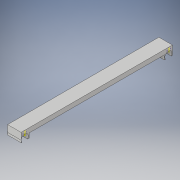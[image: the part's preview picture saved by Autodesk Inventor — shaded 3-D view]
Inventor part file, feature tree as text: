
AUTODESK INVENTOR PART (.ipt)
format: ipt  version: 2018 (Build 220112000, 112)  size: 140,288 bytes
history: native  units: in
note: dims shown in document units (in); Inventor stores cm internally (conversion verified against a paired STEP export)
features: sketch x7, extrude x4, hole x1
ambient origin geometry x8: Origin, YZ Plane, XZ Plane, XY Plane, X Axis, Y Axis, Z Axis, Center Point
bodies: Solid1 (feature_tree)
feature tree (12):
  extrude  "Extrusion1"  Depth=0.375in
  sketch  "Sketch2"  dims[d2=0.125in d3=0.0in d4=0.1in d5=0.0in]
  extrude  "Extrusion2"  Depth=0.1in TaperAngle=0.0deg
  sketch  "Sketch4"  dims[d9=0.22in d10=0.125in d11=0.0in]
  extrude  "Extrusion3"  Depth=0.22in
  extrude  "Extrusion4"  Depth=0.125in TaperAngle=0.0deg
  hole  "Hole1"  [1 undecoded]
  sketch  "Sketch1"  dims[d0=0.375in d1=4.0in]
  sketch  "Sketch3"  dims[d6=0.1in d7=0.0in d8=0.22in]
  sketch  "Sketch5"  dims[d12=0.2in]
  sketch  "Sketch6"  dims[d13=0.2in d14=0.75in d15=0.375in d16=0.25in d17=0.5635in d18=1.0in d19=0.8108in]
  sketch  "Sketch7"
note: 1 required parameter value undecoded (feature->parameter linkage not recoverable at this tier; creation-order binding heuristic only, values carry confidence <= 0.55)
